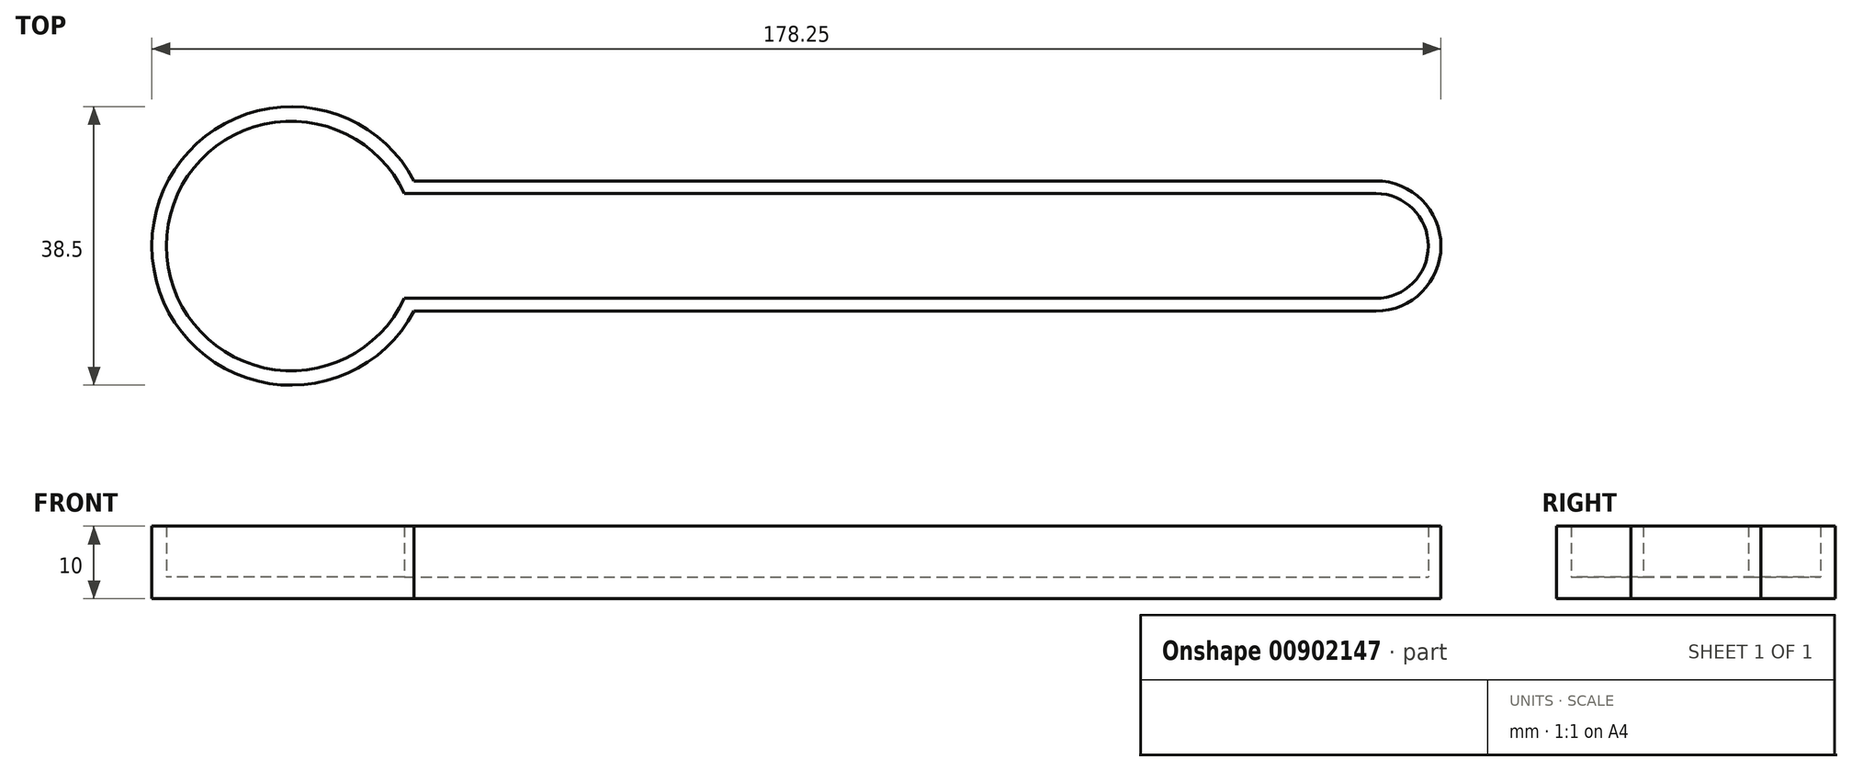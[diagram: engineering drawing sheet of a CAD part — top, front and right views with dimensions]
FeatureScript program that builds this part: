
annotation { "Feature Type Name" : "Feature", "Feature Type Description" : "" }
export const myFeature = defineFeature(function(context is Context, id is Id, definition is map)
    precondition{}
    {
        {
            var Q0;
            Q0=qCreatedBy(makeId("Top.planeOp"),FACE);
            var sketch = newSketch(context, id + "F0", { "sketchPlane" : qUnion([Q0])});
            skCircle(sketch, "E0", {"center": v(-110.87, 3.43) * mm, "radius": 5 * mm});
            skCircle(sketch, "E1.0", {"center": v(-110.87, 3.43) * mm, "radius": 7 * mm});
            skLineSegment(sketch, "E2", {"start": v(-110.87, 3.43) * mm, "end": v(39.13, 3.43) * mm});
            skCircle(sketch, "E3", {"center": v(39.13, 3.43) * mm, "radius": 5 * mm});
            skCircle(sketch, "E4.0", {"center": v(39.13, 3.43) * mm, "radius": 7 * mm});
            skLineSegment(sketch, "E5", {"start": v(39.13, 3.43) * mm, "end": v(39.13, 10.43) * mm});
            skLineSegment(sketch, "E6", {"start": v(39.13, 10.43) * mm, "end": v(39.13, 3.43) * mm});
            skLineSegment(sketch, "E7", {"start": v(39.13, -3.57) * mm, "end": v(39.13, 3.43) * mm});
            skLineSegment(sketch, "E8", {"start": v(39.13, 8.43) * mm, "end": v(39.13, -1.57) * mm});
            skCircle(sketch, "E9", {"center": v(39.13, 3.43) * mm, "radius": 9 * mm});
            skLineSegment(sketch, "E10", {"start": v(39.13, 22.38) * mm, "end": v(39.13, -5.57) * mm});
            skCircle(sketch, "E11", {"center": v(39.13, 3.43) * mm, "radius": 7.25 * mm});
            skCircle(sketch, "E12", {"center": v(-110.87, 3.43) * mm, "radius": 7.25 * mm});
            skCircle(sketch, "E13", {"center": v(-110.87, 3.43) * mm, "radius": 9 * mm});
            skLineSegment(sketch, "E14", {"start": v(-110.87, 3.43) * mm, "end": v(-110.87, 12.43) * mm});
            skLineSegment(sketch, "E15", {"start": v(-110.87, 3.43) * mm, "end": v(-110.87, -5.57) * mm});
            skLineSegment(sketch, "E16", {"start": v(39.13, 10.68) * mm, "end": v(-110.87, 10.68) * mm});
            skLineSegment(sketch, "E17", {"start": v(-110.87, 12.43) * mm, "end": v(39.13, 12.43) * mm});
            skLineSegment(sketch, "E18", {"start": v(39.13, -3.82) * mm, "end": v(-110.87, -3.82) * mm});
            skLineSegment(sketch, "E19", {"start": v(-110.87, -5.57) * mm, "end": v(39.13, -5.57) * mm});
            skCircle(sketch, "E20", {"center": v(-110.87, 3.43) * mm, "radius": 17.25 * mm});
            skCircle(sketch, "E21.0", {"center": v(-110.87, 3.43) * mm, "radius": 19.25 * mm});
            skSolve(sketch);
        }
        {
            var Q0;
            {var subQ0=sQuery(id+"F0.wireOp",EDGE,"g4Qripvs-kewp-h5Mc-p9nT-fFvRpqrIrSZP");var subQ1=sQuery(id+"F0.wireOp",EDGE,"E2");var subQ2=makeQuery(id+"F0.imprint","INTERSECT",VERTEX,{"derivedFrom":[subQ1,subQ0]});Q0=makeQuery(id+"F0.imprint","IMPRINT",FACE,{"disambiguationData":[TD([[makeQuery(id+"F0.imprint","IMPRINT",EDGE,{"disambiguationData":[TD([[subQ2,-1.0]])],"derivedFrom":subQ1}),-1.0]])]});}
            var sketch = newSketch(context, id + "F1", { "sketchPlane" : qUnion([Q0])});
            skSolve(sketch);
        }
        {
            var Q0;
            {var subQ0=sQuery(id+"F0.wireOp",EDGE,"E14");var subQ1=sQuery(id+"F0.wireOp",EDGE,"E0");var subQ2=makeQuery(id+"F0.imprint","INTERSECT",VERTEX,{"derivedFrom":[subQ1,subQ0]});Q0=makeQuery(id+"F0.imprint","IMPRINT",FACE,{"disambiguationData":[TD([[makeQuery(id+"F0.imprint","IMPRINT",EDGE,{"disambiguationData":[TD([[subQ2,1.0]])],"derivedFrom":subQ1}),1.0]])]});}
            var Q1;
            {var subQ0=sQuery(id+"F0.wireOp",EDGE,"E14");var subQ1=sQuery(id+"F0.wireOp",EDGE,"E0");var subQ2=makeQuery(id+"F0.imprint","INTERSECT",VERTEX,{"derivedFrom":[subQ1,subQ0]});Q1=makeQuery(id+"F0.imprint","IMPRINT",FACE,{"disambiguationData":[TD([[makeQuery(id+"F0.imprint","IMPRINT",EDGE,{"disambiguationData":[TD([[subQ2,-1.0]])],"derivedFrom":subQ1}),1.0]])]});}
            var Q2;
            {var subQ0=sQuery(id+"F0.wireOp",EDGE,"E2");var subQ1=sQuery(id+"F0.wireOp",EDGE,"E0");var subQ2=makeQuery(id+"F0.imprint","INTERSECT",VERTEX,{"derivedFrom":[subQ1,subQ0]});Q2=makeQuery(id+"F0.imprint","IMPRINT",FACE,{"disambiguationData":[TD([[makeQuery(id+"F0.imprint","IMPRINT",EDGE,{"disambiguationData":[TD([[subQ2,1.0]])],"derivedFrom":subQ1}),1.0]])]});}
            var Q3;
            {var subQ0=sQuery(id+"F0.wireOp",EDGE,"E2");var subQ1=sQuery(id+"F0.wireOp",EDGE,"E0");var subQ2=makeQuery(id+"F0.imprint","INTERSECT",VERTEX,{"derivedFrom":[subQ1,subQ0]});Q3=makeQuery(id+"F0.imprint","IMPRINT",FACE,{"disambiguationData":[TD([[makeQuery(id+"F0.imprint","IMPRINT",EDGE,{"disambiguationData":[TD([[subQ2,1.0]])],"derivedFrom":subQ1}),-1.0]])]});}
            var Q4;
            {var subQ0=sQuery(id+"F0.wireOp",EDGE,"E2");var subQ1=sQuery(id+"F0.wireOp",EDGE,"E1.0");var subQ2=makeQuery(id+"F0.imprint","INTERSECT",VERTEX,{"derivedFrom":[subQ1,subQ0]});Q4=makeQuery(id+"F0.imprint","IMPRINT",FACE,{"disambiguationData":[TD([[makeQuery(id+"F0.imprint","IMPRINT",EDGE,{"disambiguationData":[TD([[subQ2,1.0]])],"derivedFrom":subQ1}),-1.0]])]});}
            var Q5;
            {var subQ0=sQuery(id+"F0.wireOp",EDGE,"E12");var subQ1=sQuery(id+"F0.wireOp",EDGE,"E2");var subQ2=makeQuery(id+"F0.imprint","INTERSECT",VERTEX,{"derivedFrom":[subQ1,subQ0]});Q5=makeQuery(id+"F0.imprint","IMPRINT",FACE,{"disambiguationData":[TD([[makeQuery(id+"F0.imprint","IMPRINT",EDGE,{"disambiguationData":[TD([[subQ2,-1.0]])],"derivedFrom":subQ1}),-1.0]])]});}
            var Q6;
            {var subQ1=sQuery(id+"F0.wireOp",EDGE,"E13");var subQ3=sQuery(id+"F0.wireOp",EDGE,"E18");var subQ4=makeQuery(id+"F0.imprint","INTERSECT",VERTEX,{"derivedFrom":[subQ1,subQ3]});Q6=makeQuery(id+"F0.imprint","IMPRINT",FACE,{"disambiguationData":[TD([[makeQuery(id+"F0.imprint","IMPRINT",EDGE,{"disambiguationData":[TD([[subQ4,1.0]])],"derivedFrom":subQ1}),1.0]])]});}
            var Q7;
            {var subQ0=sQuery(id+"F0.wireOp",EDGE,"E14");var subQ1=sQuery(id+"F0.wireOp",EDGE,"E0");var subQ2=makeQuery(id+"F0.imprint","INTERSECT",VERTEX,{"derivedFrom":[subQ1,subQ0]});Q7=makeQuery(id+"F0.imprint","IMPRINT",FACE,{"disambiguationData":[TD([[makeQuery(id+"F0.imprint","IMPRINT",EDGE,{"disambiguationData":[TD([[subQ2,-1.0]])],"derivedFrom":subQ1}),-1.0]])]});}
            var Q8;
            {var subQ0=sQuery(id+"F0.wireOp",EDGE,"E14");var subQ1=sQuery(id+"F0.wireOp",EDGE,"E1.0");var subQ2=makeQuery(id+"F0.imprint","INTERSECT",VERTEX,{"derivedFrom":[subQ1,subQ0]});Q8=makeQuery(id+"F0.imprint","IMPRINT",FACE,{"disambiguationData":[TD([[makeQuery(id+"F0.imprint","IMPRINT",EDGE,{"disambiguationData":[TD([[subQ2,-1.0]])],"derivedFrom":subQ1}),-1.0]])]});}
            var Q9;
            {var subQ0=sQuery(id+"F0.wireOp",EDGE,"E14");var subQ1=sQuery(id+"F0.wireOp",EDGE,"E12");var subQ2=makeQuery(id+"F0.imprint","INTERSECT",VERTEX,{"derivedFrom":[subQ1,subQ0,sQuery(id+"F0.wireOp",EDGE,"E16")]});Q9=makeQuery(id+"F0.imprint","IMPRINT",FACE,{"disambiguationData":[TD([[makeQuery(id+"F0.imprint","IMPRINT",EDGE,{"disambiguationData":[TD([[subQ2,-1.0]])],"derivedFrom":subQ1}),-1.0]])]});}
            var Q10;
            {var subQ0=sQuery(id+"F0.wireOp",EDGE,"E14");var subQ1=sQuery(id+"F0.wireOp",EDGE,"E0");var subQ2=makeQuery(id+"F0.imprint","INTERSECT",VERTEX,{"derivedFrom":[subQ1,subQ0]});Q10=makeQuery(id+"F0.imprint","IMPRINT",FACE,{"disambiguationData":[TD([[makeQuery(id+"F0.imprint","IMPRINT",EDGE,{"disambiguationData":[TD([[subQ2,1.0]])],"derivedFrom":subQ1}),-1.0]])]});}
            var Q11;
            {var subQ0=sQuery(id+"F0.wireOp",EDGE,"E14");var subQ1=sQuery(id+"F0.wireOp",EDGE,"E1.0");var subQ2=makeQuery(id+"F0.imprint","INTERSECT",VERTEX,{"derivedFrom":[subQ1,subQ0]});Q11=makeQuery(id+"F0.imprint","IMPRINT",FACE,{"disambiguationData":[TD([[makeQuery(id+"F0.imprint","IMPRINT",EDGE,{"disambiguationData":[TD([[subQ2,1.0]])],"derivedFrom":subQ1}),-1.0]])]});}
            var Q12;
            {var subQ0=sQuery(id+"F0.wireOp",EDGE,"E12");var subQ1=sQuery(id+"F0.wireOp",EDGE,"E2");var subQ2=makeQuery(id+"F0.imprint","INTERSECT",VERTEX,{"derivedFrom":[subQ1,subQ0]});Q12=makeQuery(id+"F0.imprint","IMPRINT",FACE,{"disambiguationData":[TD([[makeQuery(id+"F0.imprint","IMPRINT",EDGE,{"disambiguationData":[TD([[subQ2,-1.0]])],"derivedFrom":subQ1}),1.0]])]});}
            var Q13;
            {var subQ1=sQuery(id+"F0.wireOp",EDGE,"E13");var subQ3=sQuery(id+"F0.wireOp",EDGE,"E16");var subQ4=makeQuery(id+"F0.imprint","INTERSECT",VERTEX,{"derivedFrom":[subQ1,subQ3]});Q13=makeQuery(id+"F0.imprint","IMPRINT",FACE,{"disambiguationData":[TD([[makeQuery(id+"F0.imprint","IMPRINT",EDGE,{"disambiguationData":[TD([[subQ4,-1.0]])],"derivedFrom":subQ1}),1.0]])]});}
            var Q14;
            {var subQ0=sQuery(id+"F0.wireOp",EDGE,"E17");Q14=makeQuery(id+"F0.imprint","IMPRINT",FACE,{"disambiguationData":[TD([[makeQuery(id+"F0.imprint","IMPRINT",EDGE,{"derivedFrom":subQ0}),-1.0]])]});}
            var Q15;
            {var subQ0=sQuery(id+"F0.wireOp",EDGE,"E13");var subQ1=sQuery(id+"F0.wireOp",EDGE,"E2");var subQ2=makeQuery(id+"F0.imprint","INTERSECT",VERTEX,{"derivedFrom":[subQ1,subQ0]});Q15=makeQuery(id+"F0.imprint","IMPRINT",FACE,{"disambiguationData":[TD([[makeQuery(id+"F0.imprint","IMPRINT",EDGE,{"disambiguationData":[TD([[subQ2,-1.0]])],"derivedFrom":subQ1}),1.0]])]});}
            var Q16;
            {var subQ0=sQuery(id+"F0.wireOp",EDGE,"E13");var subQ1=sQuery(id+"F0.wireOp",EDGE,"E2");var subQ2=makeQuery(id+"F0.imprint","INTERSECT",VERTEX,{"derivedFrom":[subQ1,subQ0]});Q16=makeQuery(id+"F0.imprint","IMPRINT",FACE,{"disambiguationData":[TD([[makeQuery(id+"F0.imprint","IMPRINT",EDGE,{"disambiguationData":[TD([[subQ2,-1.0]])],"derivedFrom":subQ1}),-1.0]])]});}
            var Q17;
            {var subQ1=sQuery(id+"F0.wireOp",EDGE,"E9");var subQ3=sQuery(id+"F0.wireOp",EDGE,"E16");var subQ4=makeQuery(id+"F0.imprint","INTERSECT",VERTEX,{"derivedFrom":[subQ1,subQ3]});Q17=makeQuery(id+"F0.imprint","IMPRINT",FACE,{"disambiguationData":[TD([[makeQuery(id+"F0.imprint","IMPRINT",EDGE,{"disambiguationData":[TD([[subQ4,1.0]])],"derivedFrom":subQ1}),1.0]])]});}
            var Q18;
            {var subQ0=sQuery(id+"F0.wireOp",EDGE,"E9");var subQ1=sQuery(id+"F0.wireOp",EDGE,"E2");var subQ2=makeQuery(id+"F0.imprint","INTERSECT",VERTEX,{"derivedFrom":[subQ1,subQ0]});Q18=makeQuery(id+"F0.imprint","IMPRINT",FACE,{"disambiguationData":[TD([[makeQuery(id+"F0.imprint","IMPRINT",EDGE,{"disambiguationData":[TD([[subQ2,-1.0]])],"derivedFrom":subQ1}),1.0]])]});}
            var Q19;
            {var subQ0=sQuery(id+"F0.wireOp",EDGE,"E11");var subQ1=sQuery(id+"F0.wireOp",EDGE,"E2");var subQ2=makeQuery(id+"F0.imprint","INTERSECT",VERTEX,{"derivedFrom":[subQ1,subQ0]});Q19=makeQuery(id+"F0.imprint","IMPRINT",FACE,{"disambiguationData":[TD([[makeQuery(id+"F0.imprint","IMPRINT",EDGE,{"disambiguationData":[TD([[subQ2,-1.0]])],"derivedFrom":subQ1}),1.0]])]});}
            var Q20;
            {var subQ0=sQuery(id+"F0.wireOp",EDGE,"E4.0");var subQ1=sQuery(id+"F0.wireOp",EDGE,"E2");var subQ2=makeQuery(id+"F0.imprint","INTERSECT",VERTEX,{"derivedFrom":[subQ1,subQ0]});Q20=makeQuery(id+"F0.imprint","IMPRINT",FACE,{"disambiguationData":[TD([[makeQuery(id+"F0.imprint","IMPRINT",EDGE,{"disambiguationData":[TD([[subQ2,-1.0]])],"derivedFrom":subQ1}),1.0]])]});}
            var Q21;
            {var subQ0=sQuery(id+"F0.wireOp",EDGE,"E10");var subQ1=sQuery(id+"F0.wireOp",EDGE,"E9");var subQ2=makeQuery(id+"F0.imprint","INTERSECT",VERTEX,{"derivedFrom":[subQ1,subQ0,sQuery(id+"F0.wireOp",EDGE,"E19")]});Q21=makeQuery(id+"F0.imprint","IMPRINT",FACE,{"disambiguationData":[TD([[makeQuery(id+"F0.imprint","IMPRINT",EDGE,{"disambiguationData":[TD([[subQ2,-1.0]])],"derivedFrom":subQ1}),1.0]])]});}
            var Q22;
            {var subQ0=sQuery(id+"F0.wireOp",EDGE,"E10");var subQ1=sQuery(id+"F0.wireOp",EDGE,"E4.0");var subQ2=makeQuery(id+"F0.imprint","INTERSECT",VERTEX,{"disambiguationData":[OD(0.0)],"derivedFrom":[subQ1,subQ0]});Q22=makeQuery(id+"F0.imprint","IMPRINT",FACE,{"disambiguationData":[TD([[makeQuery(id+"F0.imprint","IMPRINT",EDGE,{"disambiguationData":[TD([[subQ2,1.0]])],"derivedFrom":subQ1}),-1.0]])]});}
            var Q23;
            {var subQ0=sQuery(id+"F0.wireOp",EDGE,"E10");var subQ1=sQuery(id+"F0.wireOp",EDGE,"E3");var subQ2=makeQuery(id+"F0.imprint","INTERSECT",VERTEX,{"disambiguationData":[OD(0.0)],"derivedFrom":[subQ1,subQ0]});Q23=makeQuery(id+"F0.imprint","IMPRINT",FACE,{"disambiguationData":[TD([[makeQuery(id+"F0.imprint","IMPRINT",EDGE,{"disambiguationData":[TD([[subQ2,1.0]])],"derivedFrom":subQ1}),-1.0]])]});}
            var Q24;
            {var subQ0=sQuery(id+"F0.wireOp",EDGE,"E10");var subQ1=sQuery(id+"F0.wireOp",EDGE,"E2");var subQ2=makeQuery(id+"F0.imprint","INTERSECT",VERTEX,{"derivedFrom":[subQ1,subQ0]});Q24=makeQuery(id+"F1.imprint","IMPRINT",FACE,{"disambiguationData":[TD([[makeQuery(id+"F1.imprint","IMPRINT",EDGE,{"derivedFrom":makeQuery(id+"F0.imprint","IMPRINT",EDGE,{"disambiguationData":[TD([[subQ2,1.0]])],"derivedFrom":subQ1})}),-1.0]])]});}
            var Q25;
            {var subQ0=sQuery(id+"F0.wireOp",EDGE,"E9");var subQ1=sQuery(id+"F0.wireOp",EDGE,"E2");var subQ2=makeQuery(id+"F0.imprint","INTERSECT",VERTEX,{"derivedFrom":[subQ1,subQ0]});Q25=makeQuery(id+"F0.imprint","IMPRINT",FACE,{"disambiguationData":[TD([[makeQuery(id+"F0.imprint","IMPRINT",EDGE,{"disambiguationData":[TD([[subQ2,-1.0]])],"derivedFrom":subQ1}),-1.0]])]});}
            var Q26;
            {var subQ0=sQuery(id+"F0.wireOp",EDGE,"E11");var subQ1=sQuery(id+"F0.wireOp",EDGE,"E2");var subQ2=makeQuery(id+"F0.imprint","INTERSECT",VERTEX,{"derivedFrom":[subQ1,subQ0]});Q26=makeQuery(id+"F0.imprint","IMPRINT",FACE,{"disambiguationData":[TD([[makeQuery(id+"F0.imprint","IMPRINT",EDGE,{"disambiguationData":[TD([[subQ2,-1.0]])],"derivedFrom":subQ1}),-1.0]])]});}
            var Q27;
            {var subQ0=sQuery(id+"F0.wireOp",EDGE,"E4.0");var subQ1=sQuery(id+"F0.wireOp",EDGE,"E2");var subQ2=makeQuery(id+"F0.imprint","INTERSECT",VERTEX,{"derivedFrom":[subQ1,subQ0]});Q27=makeQuery(id+"F0.imprint","IMPRINT",FACE,{"disambiguationData":[TD([[makeQuery(id+"F0.imprint","IMPRINT",EDGE,{"disambiguationData":[TD([[subQ2,-1.0]])],"derivedFrom":subQ1}),-1.0]])]});}
            var Q28;
            {var subQ0=sQuery(id+"F0.wireOp",EDGE,"E10");var subQ1=sQuery(id+"F0.wireOp",EDGE,"E2");var subQ2=makeQuery(id+"F0.imprint","INTERSECT",VERTEX,{"derivedFrom":[subQ1,subQ0]});Q28=makeQuery(id+"F0.imprint","IMPRINT",FACE,{"disambiguationData":[TD([[makeQuery(id+"F0.imprint","IMPRINT",EDGE,{"disambiguationData":[TD([[subQ2,1.0]])],"derivedFrom":subQ1}),1.0]])]});}
            var Q29;
            {var subQ0=sQuery(id+"F0.wireOp",EDGE,"E10");var subQ1=sQuery(id+"F0.wireOp",EDGE,"E3");var subQ2=makeQuery(id+"F0.imprint","INTERSECT",VERTEX,{"disambiguationData":[OD(0.0)],"derivedFrom":[subQ1,subQ0]});Q29=makeQuery(id+"F0.imprint","IMPRINT",FACE,{"disambiguationData":[TD([[makeQuery(id+"F0.imprint","IMPRINT",EDGE,{"disambiguationData":[TD([[subQ2,1.0]])],"derivedFrom":subQ1}),1.0]])]});}
            var Q30;
            {var subQ1=sQuery(id+"F0.wireOp",EDGE,"E9");var subQ3=sQuery(id+"F0.wireOp",EDGE,"E18");var subQ4=makeQuery(id+"F0.imprint","INTERSECT",VERTEX,{"derivedFrom":[subQ1,subQ3]});Q30=makeQuery(id+"F0.imprint","IMPRINT",FACE,{"disambiguationData":[TD([[makeQuery(id+"F0.imprint","IMPRINT",EDGE,{"disambiguationData":[TD([[subQ4,-1.0]])],"derivedFrom":subQ1}),1.0]])]});}
            var Q31;
            {var subQ0=sQuery(id+"F0.wireOp",EDGE,"E19");Q31=makeQuery(id+"F0.imprint","IMPRINT",FACE,{"disambiguationData":[TD([[makeQuery(id+"F0.imprint","IMPRINT",EDGE,{"derivedFrom":subQ0}),1.0]])]});}
            var Q32;
            {var subQ0=sQuery(id+"F0.wireOp",EDGE,"E20");var subQ1=sQuery(id+"F0.wireOp",EDGE,"E2");var subQ2=makeQuery(id+"F0.imprint","INTERSECT",VERTEX,{"derivedFrom":[subQ1,subQ0]});Q32=makeQuery(id+"F0.imprint","IMPRINT",FACE,{"disambiguationData":[TD([[makeQuery(id+"F0.imprint","IMPRINT",EDGE,{"disambiguationData":[TD([[subQ2,-1.0]])],"derivedFrom":subQ1}),1.0]])]});}
            var Q33;
            {var subQ0=sQuery(id+"F0.wireOp",EDGE,"E20");var subQ1=sQuery(id+"F0.wireOp",EDGE,"E2");var subQ2=makeQuery(id+"F0.imprint","INTERSECT",VERTEX,{"derivedFrom":[subQ1,subQ0]});Q33=makeQuery(id+"F0.imprint","IMPRINT",FACE,{"disambiguationData":[TD([[makeQuery(id+"F0.imprint","IMPRINT",EDGE,{"disambiguationData":[TD([[subQ2,-1.0]])],"derivedFrom":subQ1}),-1.0]])]});}
            var Q34;
            {var subQ0=sQuery(id+"F0.wireOp",EDGE,"E21.0");var subQ1=sQuery(id+"F0.wireOp",EDGE,"E2");var subQ2=makeQuery(id+"F0.imprint","INTERSECT",VERTEX,{"derivedFrom":[subQ1,subQ0]});Q34=makeQuery(id+"F0.imprint","IMPRINT",FACE,{"disambiguationData":[TD([[makeQuery(id+"F0.imprint","IMPRINT",EDGE,{"disambiguationData":[TD([[subQ2,-1.0]])],"derivedFrom":subQ1}),-1.0]])]});}
            var Q35;
            {var subQ0=sQuery(id+"F0.wireOp",EDGE,"E21.0");var subQ1=sQuery(id+"F0.wireOp",EDGE,"E2");var subQ2=makeQuery(id+"F0.imprint","INTERSECT",VERTEX,{"derivedFrom":[subQ1,subQ0]});Q35=makeQuery(id+"F0.imprint","IMPRINT",FACE,{"disambiguationData":[TD([[makeQuery(id+"F0.imprint","IMPRINT",EDGE,{"disambiguationData":[TD([[subQ2,-1.0]])],"derivedFrom":subQ1}),1.0]])]});}
            var Q36;
            {var subQ0=sQuery(id+"F0.wireOp",EDGE,"E17");var subQ5=sQuery(id+"F0.wireOp",EDGE,"E20");var subQ6=makeQuery(id+"F0.imprint","INTERSECT",VERTEX,{"derivedFrom":[subQ0,subQ5]});Q36=makeQuery(id+"F0.imprint","IMPRINT",FACE,{"disambiguationData":[TD([[makeQuery(id+"F0.imprint","IMPRINT",EDGE,{"disambiguationData":[TD([[subQ6,-1.0]])],"derivedFrom":subQ5}),1.0]])]});}
            var Q37;
            {var subQ0=sQuery(id+"F0.wireOp",EDGE,"E21.0");var subQ1=sQuery(id+"F0.wireOp",EDGE,"E17");var subQ2=makeQuery(id+"F0.imprint","INTERSECT",VERTEX,{"derivedFrom":[subQ1,subQ0]});Q37=makeQuery(id+"F0.imprint","IMPRINT",FACE,{"disambiguationData":[TD([[makeQuery(id+"F0.imprint","IMPRINT",EDGE,{"disambiguationData":[TD([[subQ2,1.0]])],"derivedFrom":subQ1}),1.0]])]});}
            extrude(context, id + "F2", {"entities" : qUnion([Q0, Q1, Q2, Q3, Q4, Q5, Q6, Q7, Q8, Q9, Q10, Q11, Q12, Q13, Q14, Q15, Q16, Q17, Q18, Q19, Q20, Q21, Q22, Q23, Q24, Q25, Q26, Q27, Q28, Q29, Q30, Q31, Q32, Q33, Q34, Q35, Q36, Q37]), "depth" : 3 * mm, "offsetDistance" : 25 * mm});
        }
        {
            var Q0;
            {var subQ1=sQuery(id+"F0.wireOp",EDGE,"E9");var subQ3=sQuery(id+"F0.wireOp",EDGE,"E16");var subQ4=makeQuery(id+"F0.imprint","INTERSECT",VERTEX,{"derivedFrom":[subQ1,subQ3]});Q0=makeQuery(id+"F0.imprint","IMPRINT",FACE,{"disambiguationData":[TD([[makeQuery(id+"F0.imprint","IMPRINT",EDGE,{"disambiguationData":[TD([[subQ4,1.0]])],"derivedFrom":subQ1}),1.0]])]});}
            var Q1;
            {var subQ0=sQuery(id+"F0.wireOp",EDGE,"E10");var subQ1=sQuery(id+"F0.wireOp",EDGE,"E9");var subQ2=makeQuery(id+"F0.imprint","INTERSECT",VERTEX,{"derivedFrom":[subQ1,subQ0,sQuery(id+"F0.wireOp",EDGE,"E19")]});Q1=makeQuery(id+"F0.imprint","IMPRINT",FACE,{"disambiguationData":[TD([[makeQuery(id+"F0.imprint","IMPRINT",EDGE,{"disambiguationData":[TD([[subQ2,-1.0]])],"derivedFrom":subQ1}),1.0]])]});}
            var Q2;
            {var subQ1=sQuery(id+"F0.wireOp",EDGE,"E9");var subQ3=sQuery(id+"F0.wireOp",EDGE,"E18");var subQ4=makeQuery(id+"F0.imprint","INTERSECT",VERTEX,{"derivedFrom":[subQ1,subQ3]});Q2=makeQuery(id+"F0.imprint","IMPRINT",FACE,{"disambiguationData":[TD([[makeQuery(id+"F0.imprint","IMPRINT",EDGE,{"disambiguationData":[TD([[subQ4,-1.0]])],"derivedFrom":subQ1}),1.0]])]});}
            var Q3;
            {var subQ1=sQuery(id+"F0.wireOp",EDGE,"E9");var subQ3=sQuery(id+"F0.wireOp",EDGE,"E18");var subQ4=makeQuery(id+"F0.imprint","INTERSECT",VERTEX,{"derivedFrom":[subQ1,subQ3]});Q3=makeQuery(id+"F0.imprint","IMPRINT",FACE,{"disambiguationData":[TD([[makeQuery(id+"F0.imprint","IMPRINT",EDGE,{"disambiguationData":[TD([[subQ4,-1.0]])],"derivedFrom":subQ3}),1.0]])]});}
            var Q4;
            {var subQ1=sQuery(id+"F0.wireOp",EDGE,"E9");var subQ3=sQuery(id+"F0.wireOp",EDGE,"E16");var subQ4=makeQuery(id+"F0.imprint","INTERSECT",VERTEX,{"derivedFrom":[subQ1,subQ3]});Q4=makeQuery(id+"F0.imprint","IMPRINT",FACE,{"disambiguationData":[TD([[makeQuery(id+"F0.imprint","IMPRINT",EDGE,{"disambiguationData":[TD([[subQ4,-1.0]])],"derivedFrom":subQ3}),-1.0]])]});}
            var Q5;
            {var subQ0=sQuery(id+"F0.wireOp",EDGE,"E21.0");var subQ1=sQuery(id+"F0.wireOp",EDGE,"E16");var subQ2=makeQuery(id+"F0.imprint","INTERSECT",VERTEX,{"derivedFrom":[subQ1,subQ0]});Q5=makeQuery(id+"F0.imprint","IMPRINT",FACE,{"disambiguationData":[TD([[makeQuery(id+"F0.imprint","IMPRINT",EDGE,{"disambiguationData":[TD([[subQ2,-1.0]])],"derivedFrom":subQ1}),-1.0]])]});}
            var Q6;
            {var subQ0=sQuery(id+"F0.wireOp",EDGE,"E21.0");var subQ1=sQuery(id+"F0.wireOp",EDGE,"E17");var subQ2=makeQuery(id+"F0.imprint","INTERSECT",VERTEX,{"derivedFrom":[subQ1,subQ0]});Q6=makeQuery(id+"F0.imprint","IMPRINT",FACE,{"disambiguationData":[TD([[makeQuery(id+"F0.imprint","IMPRINT",EDGE,{"disambiguationData":[TD([[subQ2,1.0]])],"derivedFrom":subQ1}),1.0]])]});}
            var Q7;
            {var subQ0=sQuery(id+"F0.wireOp",EDGE,"E21.0");var subQ1=sQuery(id+"F0.wireOp",EDGE,"E18");var subQ2=makeQuery(id+"F0.imprint","INTERSECT",VERTEX,{"derivedFrom":[subQ1,subQ0]});Q7=makeQuery(id+"F0.imprint","IMPRINT",FACE,{"disambiguationData":[TD([[makeQuery(id+"F0.imprint","IMPRINT",EDGE,{"disambiguationData":[TD([[subQ2,-1.0]])],"derivedFrom":subQ1}),1.0]])]});}
            extrude(context, id + "F3", {"entities" : qUnion([Q0, Q1, Q2, Q3, Q4, Q5, Q6, Q7]), "operationType" : NewBodyOperationType.ADD, "depth" : 10 * mm, "offsetDistance" : 25 * mm});
        }
    });
